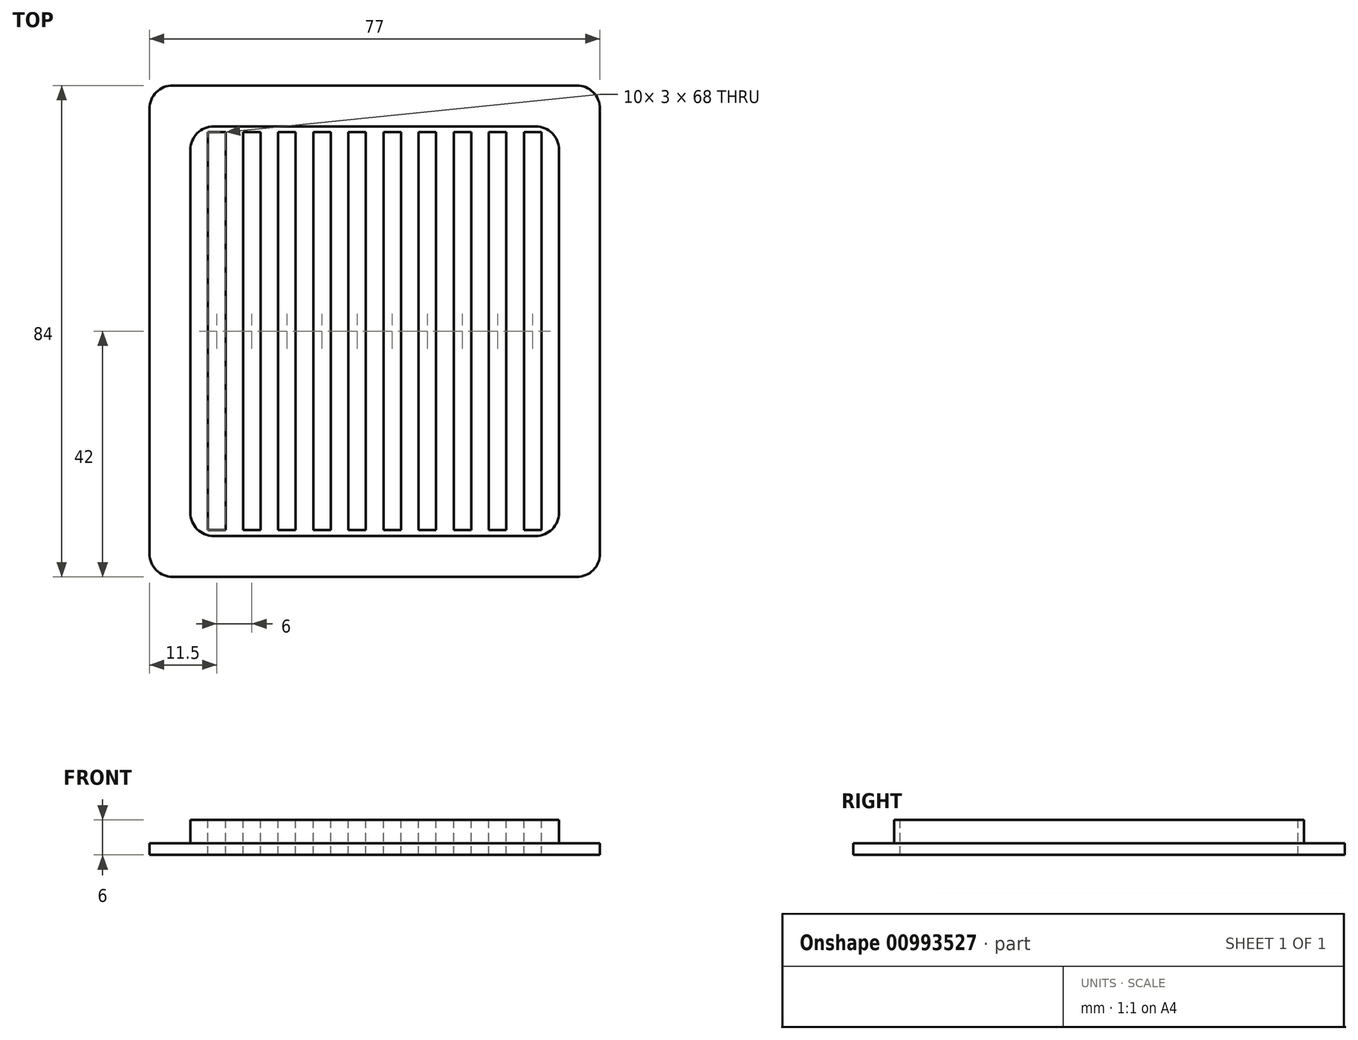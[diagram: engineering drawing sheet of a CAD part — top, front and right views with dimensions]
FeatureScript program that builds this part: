
annotation { "Feature Type Name" : "Feature", "Feature Type Description" : "" }
export const myFeature = defineFeature(function(context is Context, id is Id, definition is map)
    precondition{}
    {
        {
            var Q0;
            Q0=qCreatedBy(makeId("Top.planeOp"),FACE);
            var sketch = newSketch(context, id + "F0", { "sketchPlane" : qUnion([Q0])});
            skLineSegment(sketch, "E0.bottom", {"start": v(38.5, -42) * mm, "end": v(-38.5, -42) * mm});
            skLineSegment(sketch, "E0.top", {"start": v(38.5, 42) * mm, "end": v(-38.5, 42) * mm});
            skLineSegment(sketch, "E0.left", {"start": v(38.5, -42) * mm, "end": v(38.5, 42) * mm});
            skLineSegment(sketch, "E0.right", {"start": v(-38.5, -42) * mm, "end": v(-38.5, 42) * mm});
            skPoint(sketch, "E0.middle", {"position": v(0, 0) * mm});
            skSolve(sketch);
        }
        {
            var Q0;
            Q0=makeQuery(id+"F0.imprint","IMPRINT",FACE,{"disambiguationData":[TD([[makeQuery(id+"F0.imprint","IMPRINT",EDGE,{"derivedFrom":sQuery(id+"F0.wireOp",EDGE,"E0.bottom")}),-1.0]])]});
            extrude(context, id + "F1", {"entities" : qUnion([Q0]), "depth" : 2 * mm, "offsetDistance" : 25 * mm});
        }
        {
            var Q0;
            Q0=makeQuery(id+"F1.opExtrude","CAP_FACE",FACE,{"disambiguationData":[OSD([sQuery(id+"F0.wireOp",EDGE,"E0.bottom"),sQuery(id+"F0.wireOp",EDGE,"E0.top"),sQuery(id+"F0.wireOp",EDGE,"E0.left"),sQuery(id+"F0.wireOp",EDGE,"E0.right")])],"isStart":false});
            var sketch = newSketch(context, id + "F2", { "sketchPlane" : qUnion([Q0])});
            skLineSegment(sketch, "E1.bottom", {"start": v(31.5, -35) * mm, "end": v(-31.5, -35) * mm});
            skLineSegment(sketch, "E1.top", {"start": v(31.5, 35) * mm, "end": v(-31.5, 35) * mm});
            skLineSegment(sketch, "E1.left", {"start": v(31.5, -35) * mm, "end": v(31.5, 35) * mm});
            skLineSegment(sketch, "E1.right", {"start": v(-31.5, -35) * mm, "end": v(-31.5, 35) * mm});
            skPoint(sketch, "E1.middle", {"position": v(0, 0) * mm});
            skSolve(sketch);
        }
        {
            var Q0;
            Q0=makeQuery(id+"F2.imprint","IMPRINT",FACE,{"disambiguationData":[TD([[makeQuery(id+"F2.imprint","IMPRINT",EDGE,{"derivedFrom":sQuery(id+"F2.wireOp",EDGE,"E1.bottom")}),-1.0]])]});
            extrude(context, id + "F3", {"entities" : qUnion([Q0]), "operationType" : NewBodyOperationType.ADD, "depth" : 4 * mm, "offsetDistance" : 25 * mm});
        }
        {
            var Q0;
            Q0=makeQuery(id+"F3.opExtrude","CAP_FACE",FACE,{"disambiguationData":[OSD([sQuery(id+"F2.wireOp",EDGE,"E1.bottom"),sQuery(id+"F2.wireOp",EDGE,"E1.top"),sQuery(id+"F2.wireOp",EDGE,"E1.left"),sQuery(id+"F2.wireOp",EDGE,"E1.right")])],"isStart":false});
            var sketch = newSketch(context, id + "F4", { "sketchPlane" : qUnion([Q0])});
            skLineSegment(sketch, "E2.bottom", {"start": v(-25.5, -34) * mm, "end": v(-28.5, -34) * mm});
            skLineSegment(sketch, "E2.top", {"start": v(-25.5, 34) * mm, "end": v(-28.5, 34) * mm});
            skLineSegment(sketch, "E2.left", {"start": v(-25.5, -34) * mm, "end": v(-25.5, 34) * mm});
            skLineSegment(sketch, "E2.right", {"start": v(-28.5, -34) * mm, "end": v(-28.5, 34) * mm});
            skPoint(sketch, "E2.middle", {"position": v(0, 0) * mm});
            skLineSegment(sketch, "E3.1.0.0", {"start": v(-19.5, -34) * mm, "end": v(-19.5, 34) * mm});
            skLineSegment(sketch, "E3.1.0.1", {"start": v(-22.5, -34) * mm, "end": v(-22.5, 34) * mm});
            skLineSegment(sketch, "E3.1.0.2", {"start": v(-19.5, 34) * mm, "end": v(-22.5, 34) * mm});
            skLineSegment(sketch, "E3.1.0.3", {"start": v(-19.5, -34) * mm, "end": v(-22.5, -34) * mm});
            skLineSegment(sketch, "E3.2.0.0", {"start": v(-13.5, -34) * mm, "end": v(-13.5, 34) * mm});
            skLineSegment(sketch, "E3.2.0.1", {"start": v(-16.5, -34) * mm, "end": v(-16.5, 34) * mm});
            skLineSegment(sketch, "E3.2.0.2", {"start": v(-13.5, 34) * mm, "end": v(-16.5, 34) * mm});
            skLineSegment(sketch, "E3.2.0.3", {"start": v(-13.5, -34) * mm, "end": v(-16.5, -34) * mm});
            skLineSegment(sketch, "E3.3.0.0", {"start": v(-7.5, -34) * mm, "end": v(-7.5, 34) * mm});
            skLineSegment(sketch, "E3.3.0.1", {"start": v(-10.5, -34) * mm, "end": v(-10.5, 34) * mm});
            skLineSegment(sketch, "E3.3.0.2", {"start": v(-7.5, 34) * mm, "end": v(-10.5, 34) * mm});
            skLineSegment(sketch, "E3.3.0.3", {"start": v(-7.5, -34) * mm, "end": v(-10.5, -34) * mm});
            skLineSegment(sketch, "E3.4.0.0", {"start": v(-1.5, -34) * mm, "end": v(-1.5, 34) * mm});
            skLineSegment(sketch, "E3.4.0.1", {"start": v(-4.5, -34) * mm, "end": v(-4.5, 34) * mm});
            skLineSegment(sketch, "E3.4.0.2", {"start": v(-1.5, 34) * mm, "end": v(-4.5, 34) * mm});
            skLineSegment(sketch, "E3.4.0.3", {"start": v(-1.5, -34) * mm, "end": v(-4.5, -34) * mm});
            skLineSegment(sketch, "E3.5.0.0", {"start": v(4.5, -34) * mm, "end": v(4.5, 34) * mm});
            skLineSegment(sketch, "E3.5.0.1", {"start": v(1.5, -34) * mm, "end": v(1.5, 34) * mm});
            skLineSegment(sketch, "E3.5.0.2", {"start": v(4.5, 34) * mm, "end": v(1.5, 34) * mm});
            skLineSegment(sketch, "E3.5.0.3", {"start": v(4.5, -34) * mm, "end": v(1.5, -34) * mm});
            skLineSegment(sketch, "E3.6.0.0", {"start": v(10.5, -34) * mm, "end": v(10.5, 34) * mm});
            skLineSegment(sketch, "E3.6.0.1", {"start": v(7.5, -34) * mm, "end": v(7.5, 34) * mm});
            skLineSegment(sketch, "E3.6.0.2", {"start": v(10.5, 34) * mm, "end": v(7.5, 34) * mm});
            skLineSegment(sketch, "E3.6.0.3", {"start": v(10.5, -34) * mm, "end": v(7.5, -34) * mm});
            skLineSegment(sketch, "E3.7.0.0", {"start": v(16.5, -34) * mm, "end": v(16.5, 34) * mm});
            skLineSegment(sketch, "E3.7.0.1", {"start": v(13.5, -34) * mm, "end": v(13.5, 34) * mm});
            skLineSegment(sketch, "E3.7.0.2", {"start": v(16.5, 34) * mm, "end": v(13.5, 34) * mm});
            skLineSegment(sketch, "E3.7.0.3", {"start": v(16.5, -34) * mm, "end": v(13.5, -34) * mm});
            skLineSegment(sketch, "E3.8.0.0", {"start": v(22.5, -34) * mm, "end": v(22.5, 34) * mm});
            skLineSegment(sketch, "E3.8.0.1", {"start": v(19.5, -34) * mm, "end": v(19.5, 34) * mm});
            skLineSegment(sketch, "E3.8.0.2", {"start": v(22.5, 34) * mm, "end": v(19.5, 34) * mm});
            skLineSegment(sketch, "E3.8.0.3", {"start": v(22.5, -34) * mm, "end": v(19.5, -34) * mm});
            skLineSegment(sketch, "E3.9.0.0", {"start": v(28.5, -34) * mm, "end": v(28.5, 34) * mm});
            skLineSegment(sketch, "E3.9.0.1", {"start": v(25.5, -34) * mm, "end": v(25.5, 34) * mm});
            skLineSegment(sketch, "E3.9.0.2", {"start": v(28.5, 34) * mm, "end": v(25.5, 34) * mm});
            skLineSegment(sketch, "E3.9.0.3", {"start": v(28.5, -34) * mm, "end": v(25.5, -34) * mm});
            skLineSegment(sketch, "E3.direction1", {"start": v(-25.5, -34) * mm, "end": v(-19.5, -34) * mm, "construction": true});
            skSolve(sketch);
        }
        {
            var Q0;
            Q0=makeQuery(id+"F4.imprint","IMPRINT",FACE,{"disambiguationData":[TD([[makeQuery(id+"F4.imprint","IMPRINT",EDGE,{"derivedFrom":sQuery(id+"F4.wireOp",EDGE,"E3.5.0.0")}),1.0]])]});
            var Q1;
            Q1=makeQuery(id+"F4.imprint","IMPRINT",FACE,{"disambiguationData":[TD([[makeQuery(id+"F4.imprint","IMPRINT",EDGE,{"derivedFrom":sQuery(id+"F4.wireOp",EDGE,"E3.6.0.0")}),1.0]])]});
            var Q2;
            Q2=makeQuery(id+"F4.imprint","IMPRINT",FACE,{"disambiguationData":[TD([[makeQuery(id+"F4.imprint","IMPRINT",EDGE,{"derivedFrom":sQuery(id+"F4.wireOp",EDGE,"E3.7.0.0")}),1.0]])]});
            var Q3;
            Q3=makeQuery(id+"F4.imprint","IMPRINT",FACE,{"disambiguationData":[TD([[makeQuery(id+"F4.imprint","IMPRINT",EDGE,{"derivedFrom":sQuery(id+"F4.wireOp",EDGE,"E3.8.0.0")}),1.0]])]});
            var Q4;
            Q4=makeQuery(id+"F4.imprint","IMPRINT",FACE,{"disambiguationData":[TD([[makeQuery(id+"F4.imprint","IMPRINT",EDGE,{"derivedFrom":sQuery(id+"F4.wireOp",EDGE,"E3.9.0.0")}),1.0]])]});
            var Q5;
            Q5=makeQuery(id+"F4.imprint","IMPRINT",FACE,{"disambiguationData":[TD([[makeQuery(id+"F4.imprint","IMPRINT",EDGE,{"derivedFrom":sQuery(id+"F4.wireOp",EDGE,"E3.4.0.0")}),1.0]])]});
            var Q6;
            Q6=makeQuery(id+"F4.imprint","IMPRINT",FACE,{"disambiguationData":[TD([[makeQuery(id+"F4.imprint","IMPRINT",EDGE,{"derivedFrom":sQuery(id+"F4.wireOp",EDGE,"E3.3.0.0")}),1.0]])]});
            var Q7;
            Q7=makeQuery(id+"F4.imprint","IMPRINT",FACE,{"disambiguationData":[TD([[makeQuery(id+"F4.imprint","IMPRINT",EDGE,{"derivedFrom":sQuery(id+"F4.wireOp",EDGE,"E3.2.0.0")}),1.0]])]});
            var Q8;
            Q8=makeQuery(id+"F4.imprint","IMPRINT",FACE,{"disambiguationData":[TD([[makeQuery(id+"F4.imprint","IMPRINT",EDGE,{"derivedFrom":sQuery(id+"F4.wireOp",EDGE,"E3.1.0.0")}),1.0]])]});
            var Q9;
            Q9=makeQuery(id+"F4.imprint","IMPRINT",FACE,{"disambiguationData":[TD([[makeQuery(id+"F4.imprint","IMPRINT",EDGE,{"derivedFrom":sQuery(id+"F4.wireOp",EDGE,"E2.bottom")}),-1.0]])]});
            extrude(context, id + "F5", {"entities" : qUnion([Q0, Q1, Q2, Q3, Q4, Q5, Q6, Q7, Q8, Q9]), "operationType" : NewBodyOperationType.REMOVE, "endBound" : BoundingType.THROUGH_ALL, "oppositeDirection" : true, "depth" : 25 * mm, "offsetDistance" : 25 * mm});
        }
        {
            var Q0;
            Q0=makeQuery(id+"F1.opExtrude","SWEPT_EDGE",EDGE,{"disambiguationData":[OSD([sQuery(id+"F0.wireOp",EDGE,"E0.bottom"),sQuery(id+"F0.wireOp",EDGE,"E0.right")])]});
            var Q1;
            Q1=makeQuery(id+"F3.opExtrude","SWEPT_EDGE",EDGE,{"disambiguationData":[OSD([sQuery(id+"F2.wireOp",EDGE,"E1.bottom"),sQuery(id+"F2.wireOp",EDGE,"E1.right")])]});
            var Q2;
            Q2=makeQuery(id+"F3.opExtrude","SWEPT_EDGE",EDGE,{"disambiguationData":[OSD([sQuery(id+"F2.wireOp",EDGE,"E1.bottom"),sQuery(id+"F2.wireOp",EDGE,"E1.left")])]});
            var Q3;
            Q3=makeQuery(id+"F1.opExtrude","SWEPT_EDGE",EDGE,{"disambiguationData":[OSD([sQuery(id+"F0.wireOp",EDGE,"E0.bottom"),sQuery(id+"F0.wireOp",EDGE,"E0.left")])]});
            var Q4;
            Q4=makeQuery(id+"F3.opExtrude","SWEPT_EDGE",EDGE,{"disambiguationData":[OSD([sQuery(id+"F2.wireOp",EDGE,"E1.top"),sQuery(id+"F2.wireOp",EDGE,"E1.right")])]});
            var Q5;
            Q5=makeQuery(id+"F1.opExtrude","SWEPT_EDGE",EDGE,{"disambiguationData":[OSD([sQuery(id+"F0.wireOp",EDGE,"E0.top"),sQuery(id+"F0.wireOp",EDGE,"E0.right")])]});
            var Q6;
            Q6=makeQuery(id+"F3.opExtrude","SWEPT_EDGE",EDGE,{"disambiguationData":[OSD([sQuery(id+"F2.wireOp",EDGE,"E1.top"),sQuery(id+"F2.wireOp",EDGE,"E1.left")])]});
            var Q7;
            Q7=makeQuery(id+"F1.opExtrude","SWEPT_EDGE",EDGE,{"disambiguationData":[OSD([sQuery(id+"F0.wireOp",EDGE,"E0.top"),sQuery(id+"F0.wireOp",EDGE,"E0.left")])]});
            fillet(context, id + "F6", {"entities" : qUnion([Q0, Q1, Q2, Q3, Q4, Q5, Q6, Q7]), "radius" : 4 * mm, "tangentPropagation" : true, "allowEdgeOverflow" : false});
        }
    });
